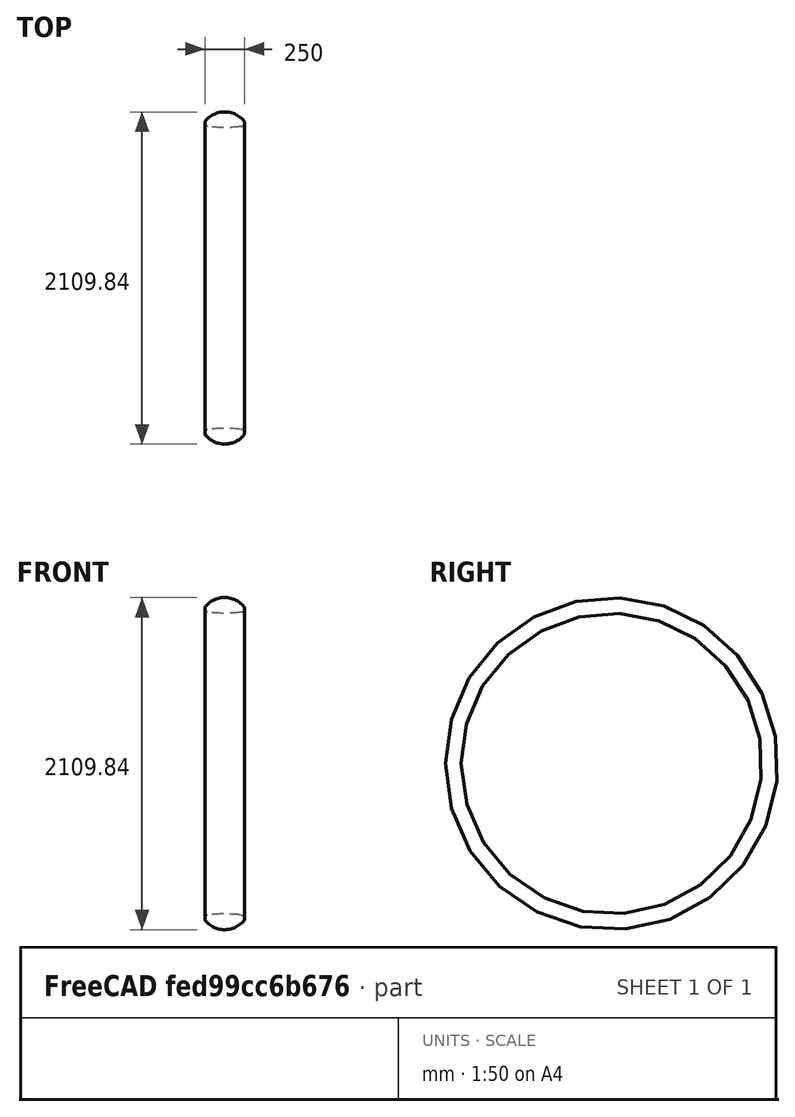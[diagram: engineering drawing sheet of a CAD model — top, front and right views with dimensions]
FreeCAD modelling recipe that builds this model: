
FCSTD DOCUMENT
Label: PR_002
objects: Sketcher::SketchObject×1, PartDesign::Revolution×1
note: 3 computed .brp shape members not serialized (recipe doc carries the construction recipe); baked Part::Feature solids carry a one-line shape summary decoded from their .brp

FEATURE [Sketcher::SketchObject] Sketch
  sketch-geometry (10):
    g0: LineSegment [constr] StartX=-194.452 StartY=-954.92 StartZ=0 EndX=551.146 EndY=-954.92 EndZ=0
    g1: LineSegment StartX=0 StartY=-982.511 StartZ=0 EndX=0 EndY=-985.612 EndZ=0
    g2: LineSegment StartX=250 StartY=-982.511 StartZ=0 EndX=250 EndY=-985.612 EndZ=0
    g3: LineSegment [constr] StartX=-263.211 StartY=-1054.92 StartZ=0 EndX=396.606 EndY=-1054.92 EndZ=0
    g4: ArcOfCircle CenterX=20 CenterY=-982.511 CenterZ=0 NormalX=0 NormalY=0 NormalZ=1 Radius=20 StartAngle=1.71513 EndAngle=3.14159
    g5: ArcOfCircle CenterX=230 CenterY=-982.511 CenterZ=0 NormalX=0 NormalY=0 NormalZ=1 Radius=20 StartAngle=0 EndAngle=1.42646
    g6: ArcOfCircle CenterX=225 CenterY=-985.612 CenterZ=0 NormalX=0 NormalY=0 NormalZ=1 Radius=25 StartAngle=5.54656 EndAngle=6.28319
    g7: ArcOfCircle CenterX=25 CenterY=-985.612 CenterZ=0 NormalX=0 NormalY=0 NormalZ=1 Radius=25 StartAngle=3.14159 EndAngle=3.87822
    g8: ArcOfCircle CenterX=125 CenterY=-894.92 CenterZ=0 NormalX=0 NormalY=0 NormalZ=1 Radius=160 StartAngle=3.87822 EndAngle=5.54656
    g9: ArcOfCircle CenterX=125 CenterY=-1704.92 CenterZ=0 NormalX=0 NormalY=0 NormalZ=1 Radius=750 StartAngle=1.42646 EndAngle=1.71513
  constraints (30):
    c: Horizontal(g0)
    c: DistanceY(g0) = -954.92
    c: Vertical(g1)
    c: Vertical(g2)
    c: DistanceX(g1) = 0
    c: DistanceX(g1,g2) = 250
    c: Horizontal(g3)
    c: DistanceY(g0,g3) = -100
    c: Radius(g4) = 20
    c: Radius(g5) = 20
    c: Radius(g6) = 25
    c: Radius(g7) = 25
    c: Tangent(g4,g1)
    c: Tangent(g5,g2)
    c: Tangent(g6,g2)
    c: Tangent(g1,g7)
    c: Tangent(g7,g8)
    c: Tangent(g8,g6)
    c: Tangent(g3,g8)
    c: Radius(g8) = 160
    c: Radius(g9) = 750
    c: Tangent(g4,g9)
    c: Tangent(g9,g5)
    c: Tangent(g0,g9)
    c: DistanceX(g8) = 125
    c: DistanceX(g9) = 125
    c: DistanceX(g3) = -263.211
    c: DistanceX(g0) = -194.452
    c: DistanceX(g0) = 551.146
    c: DistanceX(g3) = 396.606
FEATURE [PartDesign::Revolution] Revolution
  Angle = 360
  Axis = (1,0,0)
  Base = (0,0,0)
  ReferenceAxis = -> Sketch [H_Axis]
  Sketch = -> Sketch
